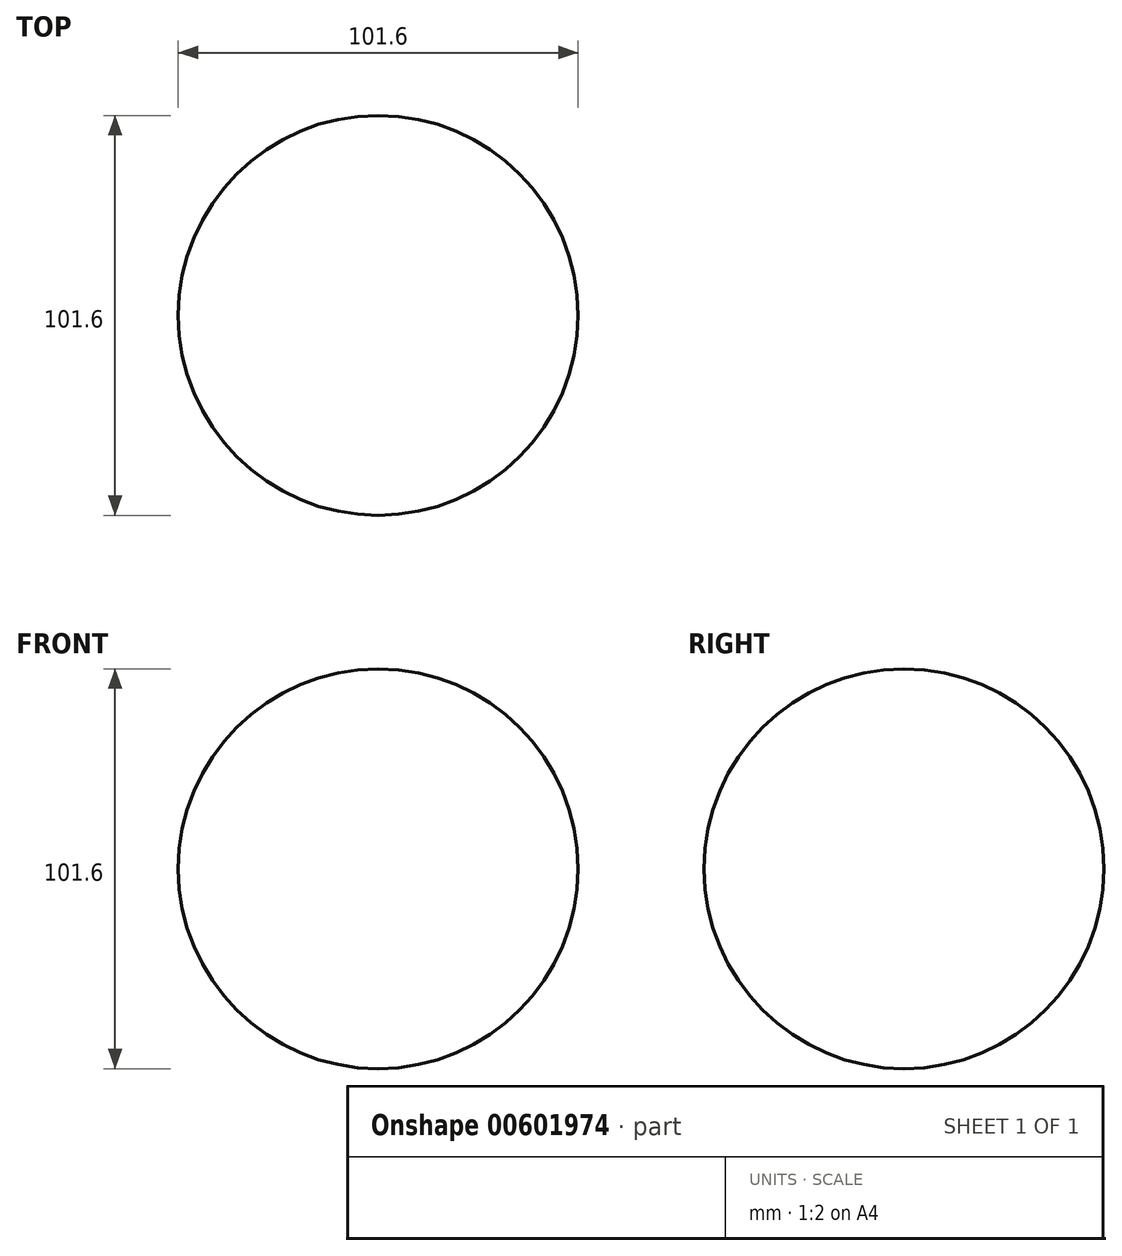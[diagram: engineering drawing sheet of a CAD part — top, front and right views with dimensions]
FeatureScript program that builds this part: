
annotation { "Feature Type Name" : "Feature", "Feature Type Description" : "" }
export const myFeature = defineFeature(function(context is Context, id is Id, definition is map)
    precondition{}
    {
        {
            var Q0;
            Q0=qCreatedBy(makeId("Front.planeOp"),FACE);
            var sketch = newSketch(context, id + "F0", { "sketchPlane" : qUnion([Q0])});
            skCircle(sketch, "E0", {"center": v(0, 0) * mm, "radius": 50.8 * mm});
            skLineSegment(sketch, "E1", {"start": v(0, 63.34) * mm, "end": v(0, -72.27) * mm});
            skSolve(sketch);
        }
        {
            var Q0;
            {var subQ0=sQuery(id+"F0.wireOp",EDGE,"E1");var subQ1=sQuery(id+"F0.wireOp",EDGE,"E0");var subQ2=makeQuery(id+"F0.imprint","INTERSECT",VERTEX,{"disambiguationData":[OD(0.0)],"derivedFrom":[subQ1,subQ0]});Q0=makeQuery(id+"F0.imprint","IMPRINT",FACE,{"disambiguationData":[TD([[makeQuery(id+"F0.imprint","IMPRINT",EDGE,{"disambiguationData":[TD([[subQ2,1.0]])],"derivedFrom":subQ1}),1.0]])]});}
            var Q1;
            Q1=sQuery(id+"F0.wireOp",EDGE,"E1");
            revolve(context, id + "F1", {"entities" : qUnion([Q0]), "axis" : qUnion([Q1]), "revolveType" : RevolveType.FULL});
        }
    });
